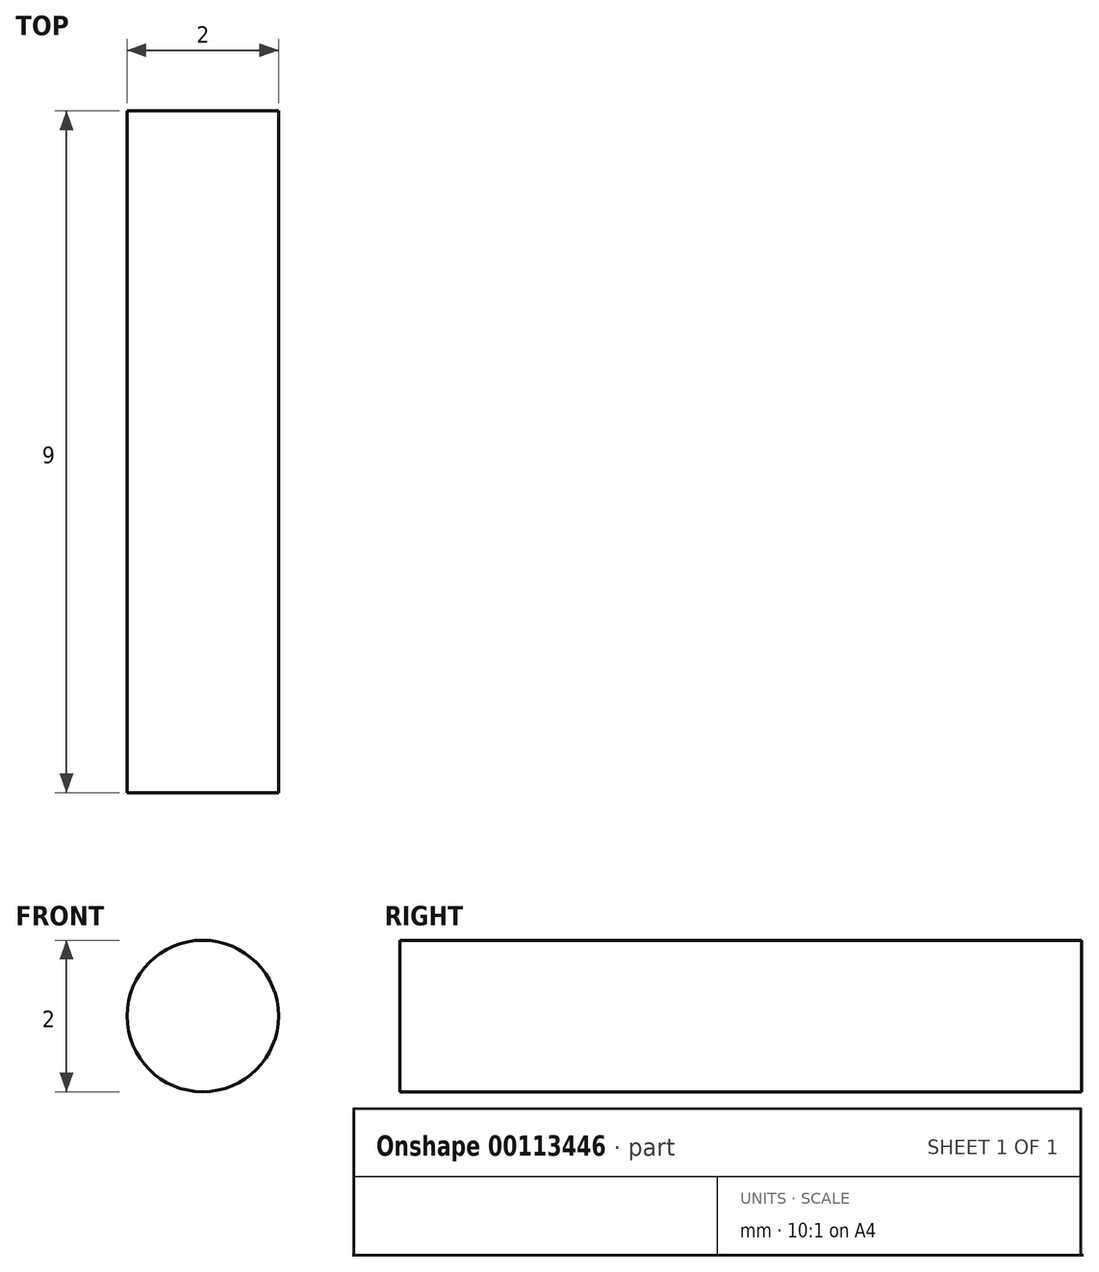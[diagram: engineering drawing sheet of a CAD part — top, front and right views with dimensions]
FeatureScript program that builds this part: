
annotation { "Feature Type Name" : "Feature", "Feature Type Description" : "" }
export const myFeature = defineFeature(function(context is Context, id is Id, definition is map)
    precondition{}
    {
        {
            var Q0;
            Q0=qCreatedBy(makeId("Front.planeOp"),FACE);
            var sketch = newSketch(context, id + "F0", { "sketchPlane" : qUnion([Q0])});
            skCircle(sketch, "E0", {"center": v(0, 0) * mm, "radius": 1 * mm});
            skSolve(sketch);
        }
        {
            var Q0;
            Q0=makeQuery(id+"F0.imprint","IMPRINT",FACE,{"disambiguationData":[TD([[makeQuery(id+"F0.imprint","IMPRINT",EDGE,{"derivedFrom":sQuery(id+"F0.wireOp",EDGE,"E0")}),1.0]])]});
            extrude(context, id + "F1", {"entities" : qUnion([Q0]), "depth" : 9 * mm});
        }
    });
